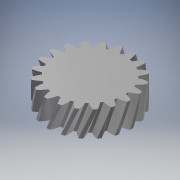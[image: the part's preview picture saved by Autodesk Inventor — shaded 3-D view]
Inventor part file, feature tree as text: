
AUTODESK INVENTOR PART (.ipt)
format: ipt  version: 2017 SP1 (Build 210196100, 196)  size: 379,392 bytes
history: native  units: mm (DEFAULTED — no unit token found)
features: plane x3, other x3, sketch x2, extrude x1
ambient origin geometry x8: Origin, YZ Plane, XZ Plane, XY Plane, X Axis, Y Axis, Z Axis, Center Point
bodies: Solid1 (feature_tree)
feature tree (9):
  extrude  "Extrusion1"  Depth=10.0mm TaperAngle=0.0deg
  plane  "Work Plane2"
  plane  "Work Plane8"
  plane  "Work Plane9"
  other  "Engrenage cylindrique"
  sketch  "Sketch1"  dims[d0=32.749068mm d1=10.0mm d2=0.0mm]
  sketch  "Sketch2"  dims[d3=30.066593mm d4=10.0mm d5=0.0mm d16=30.066593mm d17=0.0mm d34=1.570796mm d39=0.0mm d41=0.0mm d43=30.066593mm d46=30.066593mm d47=0.0mm d48=0.0mm]
  other  "Srf1"
  other  "Diamètre primitif"
